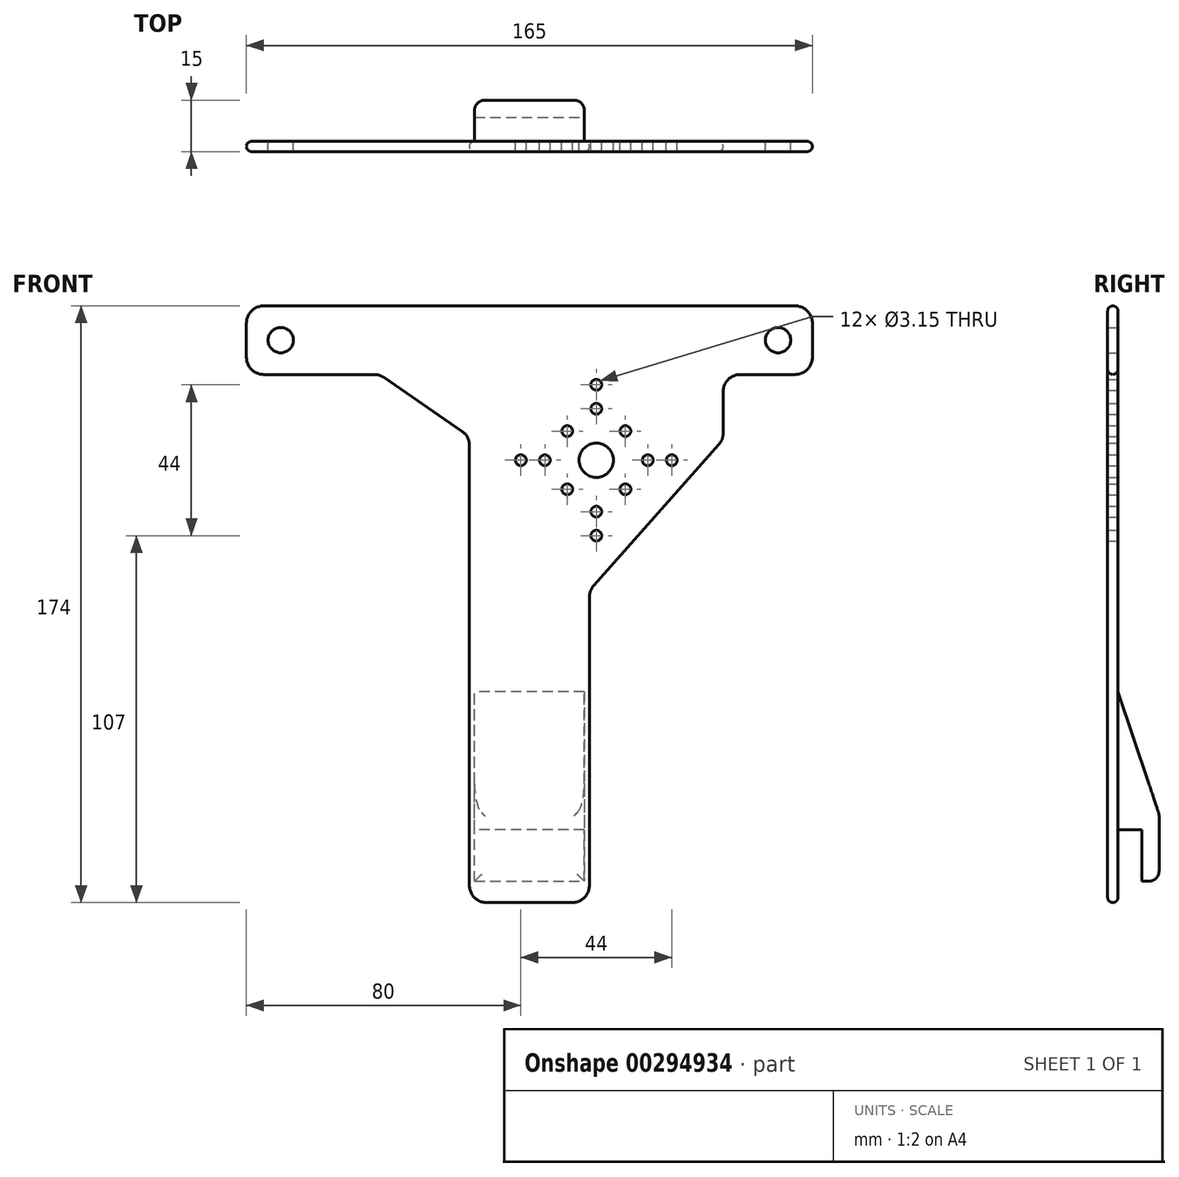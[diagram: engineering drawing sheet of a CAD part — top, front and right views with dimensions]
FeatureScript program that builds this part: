
annotation { "Feature Type Name" : "Feature", "Feature Type Description" : "" }
export const myFeature = defineFeature(function(context is Context, id is Id, definition is map)
    precondition{}
    {
        {
            var Q0;
            Q0=qCreatedBy(makeId("Front.planeOp"),FACE);
            var sketch = newSketch(context, id + "F0", { "sketchPlane" : qUnion([Q0])});
            skPoint(sketch, "E0.middle", {"position": v(0, 0) * mm});
            skLineSegment(sketch, "E1", {"start": v(82.5, 40) * mm, "end": v(-82.5, 40) * mm, "construction": true});
            skCircle(sketch, "E2", {"center": v(19.5, 33) * mm, "radius": 5 * mm});
            skCircle(sketch, "E3", {"center": v(41.5, 33) * mm, "radius": 1.57 * mm});
            skCircle(sketch, "E4", {"center": v(34.5, 33) * mm, "radius": 1.57 * mm});
            skCircle(sketch, "E5", {"center": v(19.5, 11) * mm, "radius": 1.57 * mm});
            skCircle(sketch, "E6", {"center": v(19.5, 18) * mm, "radius": 1.57 * mm});
            skLineSegment(sketch, "E7", {"start": v(19.5, 63.47) * mm, "end": v(19.5, 5.45) * mm, "construction": true});
            skCircle(sketch, "E8.MirrorC", {"center": v(-2.5, 33) * mm, "radius": 1.57 * mm});
            skCircle(sketch, "E9.MirrorC", {"center": v(4.5, 33) * mm, "radius": 1.57 * mm});
            skCircle(sketch, "E10.MirrorC", {"center": v(19.5, 55) * mm, "radius": 1.57 * mm});
            skCircle(sketch, "E11.MirrorC", {"center": v(19.5, 48) * mm, "radius": 1.57 * mm});
            skLineSegment(sketch, "E12", {"start": v(19.5, 40) * mm, "end": v(0.9, 58.6) * mm, "construction": true});
            skCircle(sketch, "E13", {"center": v(11.01, 41.49) * mm, "radius": 1.57 * mm});
            skCircle(sketch, "E14.MirrorC", {"center": v(27.99, 41.49) * mm, "radius": 1.57 * mm});
            skCircle(sketch, "E15.MirrorC", {"center": v(27.99, 24.51) * mm, "radius": 1.57 * mm});
            skCircle(sketch, "E16.MirrorC", {"center": v(11.01, 24.51) * mm, "radius": 1.57 * mm});
            skLineSegment(sketch, "E17", {"start": v(-82.5, -80) * mm, "end": v(82.5, -80) * mm, "construction": true});
            skLineSegment(sketch, "E18", {"start": v(-17.5, -80) * mm, "end": v(-17.5, -91) * mm});
            skLineSegment(sketch, "E19", {"start": v(17.5, -80) * mm, "end": v(17.5, -91) * mm});
            skLineSegment(sketch, "E20", {"start": v(17.5, -80) * mm, "end": v(17.5, -6.9) * mm});
            skLineSegment(sketch, "E21", {"start": v(56.5, 40.9) * mm, "end": v(56.5, 53) * mm});
            skPoint(sketch, "E22.visualSharp", {"position": v(-82.5, 78) * mm});
            skPoint(sketch, "E23.visualSharp", {"position": v(17.5, 0) * mm});
            skLineSegment(sketch, "E24", {"start": v(-12.5, -96) * mm, "end": v(12.5, -96) * mm});
            skPoint(sketch, "E25.visualSharp", {"position": v(-17.5, -96) * mm});
            skArc(sketch, "E25.filletArc", {"start": v(-17.5, -91) * mm, "mid": v(-16.04, -94.54) * mm, "end": v(-12.5, -96) * mm});
            skPoint(sketch, "E26.visualSharp", {"position": v(17.5, -96) * mm});
            skArc(sketch, "E26.filletArc", {"start": v(12.5, -96) * mm, "mid": v(16.04, -94.54) * mm, "end": v(17.5, -91) * mm});
            skLineSegment(sketch, "E27", {"start": v(18.76, -3.58) * mm, "end": v(55.24, 37.58) * mm});
            skPoint(sketch, "E28.visualSharp", {"position": v(56.5, 39) * mm});
            skArc(sketch, "E28.filletArc", {"start": v(55.24, 37.58) * mm, "mid": v(56.17, 39.12) * mm, "end": v(56.5, 40.9) * mm});
            skPoint(sketch, "E29.visualSharp", {"position": v(17.5, -5) * mm});
            skArc(sketch, "E29.filletArc", {"start": v(18.76, -3.58) * mm, "mid": v(17.83, -5.12) * mm, "end": v(17.5, -6.9) * mm});
            skCircle(sketch, "E30", {"center": v(-72.5, 68) * mm, "radius": 3.68 * mm});
            skCircle(sketch, "E31", {"center": v(72.5, 68) * mm, "radius": 3.68 * mm});
            skLineSegment(sketch, "E32", {"start": v(82.5, 73) * mm, "end": v(82.5, 63) * mm});
            skLineSegment(sketch, "E33", {"start": v(-82.5, 73) * mm, "end": v(-82.5, 63) * mm});
            skLineSegment(sketch, "E34", {"start": v(-77.5, 78) * mm, "end": v(77.5, 78) * mm});
            skLineSegment(sketch, "E35.trimOffspring", {"start": v(61.5, 58) * mm, "end": v(77.5, 58) * mm});
            skPoint(sketch, "E36.visualSharp", {"position": v(-82.5, 58) * mm});
            skArc(sketch, "E36.filletArc", {"start": v(-82.5, 63) * mm, "mid": v(-81.04, 59.46) * mm, "end": v(-77.5, 58) * mm});
            skArc(sketch, "E37.filletArc", {"start": v(-77.5, 78) * mm, "mid": v(-81.04, 76.54) * mm, "end": v(-82.5, 73) * mm});
            skPoint(sketch, "E38.visualSharp", {"position": v(82.5, 78) * mm});
            skArc(sketch, "E38.filletArc", {"start": v(82.5, 73) * mm, "mid": v(81.04, 76.54) * mm, "end": v(77.5, 78) * mm});
            skPoint(sketch, "E39.visualSharp", {"position": v(82.5, 58) * mm});
            skArc(sketch, "E39.filletArc", {"start": v(77.5, 58) * mm, "mid": v(81.04, 59.46) * mm, "end": v(82.5, 63) * mm});
            skPoint(sketch, "E40.visualSharp", {"position": v(56.5, 58) * mm});
            skArc(sketch, "E40.filletArc", {"start": v(61.5, 58) * mm, "mid": v(57.96, 56.54) * mm, "end": v(56.5, 53) * mm});
            skLineSegment(sketch, "E41", {"start": v(-77.5, 58) * mm, "end": v(-45.3, 58) * mm});
            skLineSegment(sketch, "E42", {"start": v(-17.5, -80) * mm, "end": v(-17.5, 37.37) * mm});
            skLineSegment(sketch, "E43", {"start": v(-42.47, 57.12) * mm, "end": v(-19.67, 41.49) * mm});
            skPoint(sketch, "E44.visualSharp", {"position": v(-43.75, 58) * mm});
            skArc(sketch, "E44.filletArc", {"start": v(-42.47, 57.12) * mm, "mid": v(-43.82, 57.78) * mm, "end": v(-45.3, 58) * mm});
            skPoint(sketch, "E45.visualSharp", {"position": v(-17.5, 40) * mm});
            skArc(sketch, "E45.filletArc", {"start": v(-17.5, 37.37) * mm, "mid": v(-18.08, 39.7) * mm, "end": v(-19.67, 41.49) * mm});
            skSolve(sketch);
        }
        {
            var Q0;
            Q0=makeQuery(id+"F0.imprint","IMPRINT",FACE,{"disambiguationData":[TD([[makeQuery(id+"F0.imprint","IMPRINT",EDGE,{"derivedFrom":sQuery(id+"F0.wireOp",EDGE,"E0.top")}),1.0]])]});
            var Q1;
            Q1=makeQuery(id+"F0.imprint","IMPRINT",FACE,{"disambiguationData":[TD([[makeQuery(id+"F0.imprint","IMPRINT",EDGE,{"derivedFrom":sQuery(id+"F0.wireOp",EDGE,"E2")}),-1.0]])]});
            extrude(context, id + "F1", {"entities" : qUnion([Q0, Q1]), "depth" : 3 * mm, "offsetDistance" : 25 * mm});
        }
        {
            var Q0;
            Q0=makeQuery(id+"F1.opExtrude","CAP_EDGE",EDGE,{"disambiguationData":[OSD([sQuery(id+"F0.wireOp",EDGE,"E34")])],"isStart":true});
            var Q1;
            Q1=makeQuery(id+"F1.opExtrude","CAP_EDGE",EDGE,{"disambiguationData":[OSD([sQuery(id+"F0.wireOp",EDGE,"E34")])],"isStart":false});
            fillet(context, id + "F2", {"entities" : qUnion([Q0, Q1]), "radius" : 1.5 * mm, "tangentPropagation" : true, "allowEdgeOverflow" : false});
        }
        {
            var Q0;
            Q0=makeQuery(id+"F1.opExtrude","CAP_FACE",FACE,{"disambiguationData":[OSD([sQuery(id+"F0.wireOp",EDGE,"E0.top"),sQuery(id+"F0.wireOp",EDGE,"E2"),sQuery(id+"F0.wireOp",EDGE,"E3"),sQuery(id+"F0.wireOp",EDGE,"E4"),sQuery(id+"F0.wireOp",EDGE,"E5"),sQuery(id+"F0.wireOp",EDGE,"E6"),sQuery(id+"F0.wireOp",EDGE,"E8.MirrorC"),sQuery(id+"F0.wireOp",EDGE,"E9.MirrorC"),sQuery(id+"F0.wireOp",EDGE,"E10.MirrorC"),sQuery(id+"F0.wireOp",EDGE,"E11.MirrorC"),sQuery(id+"F0.wireOp",EDGE,"E13"),sQuery(id+"F0.wireOp",EDGE,"E14.MirrorC"),sQuery(id+"F0.wireOp",EDGE,"E15.MirrorC"),sQuery(id+"F0.wireOp",EDGE,"E16.MirrorC"),sQuery(id+"F0.wireOp",EDGE,"n9Zw0jRa-YzkP-SSRb-jX76-UWUrNYys0Myr"),sQuery(id+"F0.wireOp",EDGE,"6nXTgwqW-IkDt-4185-NQ3I-D9ohkwow1pDC"),sQuery(id+"F0.wireOp",EDGE,"fnSGR3eZ-Ceom-D6FO-QKlf-8HLsdzlY8Ce6"),sQuery(id+"F0.wireOp",EDGE,"E18"),sQuery(id+"F0.wireOp",EDGE,"E19"),sQuery(id+"F0.wireOp",EDGE,"8tiRwyeG-NVE4-zL7y-cv12-UPCtmKI0cug2"),sQuery(id+"F0.wireOp",EDGE,"E20"),sQuery(id+"F0.wireOp",EDGE,"ygad2Ens-O4ax-aDfu-Q5ng-kWepvQ1ZYTQx"),sQuery(id+"F0.wireOp",EDGE,"E21"),sQuery(id+"F0.wireOp",EDGE,"29b9c4b6-7081-4e3b-b4dd-28010079924f.trimOffspring"),sQuery(id+"F0.wireOp",EDGE,"4647f22d-6d82-4992-9f22-0e3dd7c63f78.trimOffspring"),sQuery(id+"F0.wireOp",EDGE,"0a04f032-77e3-4663-9b60-4ac6a7c6c2fa.trimOffspring"),sQuery(id+"F0.wireOp",EDGE,"5f09185c-aee7-4edb-8201-1ebfa4ec7862.filletArc"),sQuery(id+"F0.wireOp",EDGE,"E22.filletArc"),sQuery(id+"F0.wireOp",EDGE,"c5754e04-9c71-4b08-b6d4-417d1572ddd7.filletArc"),sQuery(id+"F0.wireOp",EDGE,"7fc32371-5d91-4005-95ad-299b1605f1e9.filletArc"),sQuery(id+"F0.wireOp",EDGE,"473fdc03-1da2-4e76-872e-939869ff3119.filletArc"),sQuery(id+"F0.wireOp",EDGE,"168d16bf-a7e2-44a5-a079-a20fe12f3d41.filletArc"),sQuery(id+"F0.wireOp",EDGE,"bfc25fbe-79ac-433f-8260-2f5cbf39e1db.filletArc"),sQuery(id+"F0.wireOp",EDGE,"E23.filletArc"),sQuery(id+"F0.wireOp",EDGE,"E24"),sQuery(id+"F0.wireOp",EDGE,"E25.filletArc"),sQuery(id+"F0.wireOp",EDGE,"E26.filletArc")])],"isStart":true});
            var sketch = newSketch(context, id + "F3", { "sketchPlane" : qUnion([Q0])});
            skLineSegment(sketch, "E46", {"start": v(-16, -74.8) * mm, "end": v(16, -74.8) * mm});
            skLineSegment(sketch, "E47", {"start": v(16, -74.8) * mm, "end": v(16, -70.22) * mm});
            skLineSegment(sketch, "E48", {"start": v(16, -70.22) * mm, "end": v(-16, -70.22) * mm});
            skLineSegment(sketch, "E49", {"start": v(-16, -70.22) * mm, "end": v(-16, -74.8) * mm});
            skSolve(sketch);
        }
        {
            var Q0;
            Q0 = qSketchRegion(id + "F3", true);
            extrude(context, id + "F4", {"entities" : qUnion([Q0]), "operationType" : NewBodyOperationType.ADD, "depth" : 12 * mm, "offsetDistance" : 25 * mm});
        }
        {
            var Q0;
            Q0=makeQuery(id+"F4.opExtrude","SWEPT_FACE",FACE,{"disambiguationData":[OSD([sQuery(id+"F3.wireOp",EDGE,"E46")])]});
            var sketch = newSketch(context, id + "F5", { "sketchPlane" : qUnion([Q0])});
            skLineSegment(sketch, "E50.bottom", {"start": v(-16, -12) * mm, "end": v(16, -12) * mm});
            skLineSegment(sketch, "E50.top", {"start": v(-16, -7) * mm, "end": v(16, -7) * mm});
            skLineSegment(sketch, "E50.left", {"start": v(-16, -12) * mm, "end": v(-16, -7) * mm});
            skLineSegment(sketch, "E50.right", {"start": v(16, -12) * mm, "end": v(16, -7) * mm});
            skSolve(sketch);
        }
        {
            var Q0;
            Q0=makeQuery(id+"F5.imprint","IMPRINT",FACE,{"disambiguationData":[TD([[makeQuery(id+"F5.imprint","IMPRINT",EDGE,{"derivedFrom":sQuery(id+"F5.wireOp",EDGE,"E50.bottom")}),-1.0]])]});
            extrude(context, id + "F6", {"entities" : qUnion([Q0]), "operationType" : NewBodyOperationType.ADD, "depth" : 15 * mm});
        }
        {
            var Q0;
            Q0=makeQuery(id+"F6.boolean.opBoolean","MERGE",FACE,{"derivedFrom":[makeQuery(id+"F4.opExtrude","SWEPT_FACE",FACE,{"disambiguationData":[OSD([sQuery(id+"F3.wireOp",EDGE,"E47")])]}),makeQuery(id+"F6.opExtrude","SWEPT_FACE",FACE,{"disambiguationData":[OSD([sQuery(id+"F5.wireOp",EDGE,"E50.left")])]})]});
            var sketch = newSketch(context, id + "F7", { "sketchPlane" : qUnion([Q0])});
            skLineSegment(sketch, "E51", {"start": v(-12, -70.22) * mm, "end": v(0, -34.5) * mm});
            skLineSegment(sketch, "E52", {"start": v(0, -34.5) * mm, "end": v(0, -70.22) * mm});
            skSolve(sketch);
        }
        {
            var Q0;
            Q0=makeQuery(id+"F7.imprint","IMPRINT",FACE,{"disambiguationData":[TD([[makeQuery(id+"F7.imprint","IMPRINT",EDGE,{"derivedFrom":sQuery(id+"F7.wireOp",EDGE,"E51")}),-1.0]])]});
            extrude(context, id + "F8", {"entities" : qUnion([Q0]), "operationType" : NewBodyOperationType.ADD, "oppositeDirection" : true, "depth" : 32 * mm, "offsetDistance" : 25 * mm});
        }
        {
            var Q0;
            {var subQ0=sQuery(id+"F3.wireOp",EDGE,"E48");Q0=makeQuery(id+"F8.boolean.opBoolean","MERGE",EDGE,{"derivedFrom":[makeQuery(id+"F4.opExtrude","CAP_EDGE",EDGE,{"disambiguationData":[OSD([subQ0])],"isStart":false}),makeQuery(id+"F8.opExtrude","SWEPT_EDGE",EDGE,{"disambiguationData":[OSD([sQuery(id+"F0.wireOp",EDGE,"E0.top"),sQuery(id+"F0.wireOp",EDGE,"E2"),sQuery(id+"F0.wireOp",EDGE,"E3"),sQuery(id+"F0.wireOp",EDGE,"E4"),sQuery(id+"F0.wireOp",EDGE,"E5"),sQuery(id+"F0.wireOp",EDGE,"E6"),sQuery(id+"F0.wireOp",EDGE,"E8.MirrorC"),sQuery(id+"F0.wireOp",EDGE,"E9.MirrorC"),sQuery(id+"F0.wireOp",EDGE,"E10.MirrorC"),sQuery(id+"F0.wireOp",EDGE,"E11.MirrorC"),sQuery(id+"F0.wireOp",EDGE,"E13"),sQuery(id+"F0.wireOp",EDGE,"E14.MirrorC"),sQuery(id+"F0.wireOp",EDGE,"E15.MirrorC"),sQuery(id+"F0.wireOp",EDGE,"E16.MirrorC"),sQuery(id+"F0.wireOp",EDGE,"n9Zw0jRa-YzkP-SSRb-jX76-UWUrNYys0Myr"),sQuery(id+"F0.wireOp",EDGE,"6nXTgwqW-IkDt-4185-NQ3I-D9ohkwow1pDC"),sQuery(id+"F0.wireOp",EDGE,"fnSGR3eZ-Ceom-D6FO-QKlf-8HLsdzlY8Ce6"),sQuery(id+"F0.wireOp",EDGE,"E18"),sQuery(id+"F0.wireOp",EDGE,"E19"),sQuery(id+"F0.wireOp",EDGE,"8tiRwyeG-NVE4-zL7y-cv12-UPCtmKI0cug2"),sQuery(id+"F0.wireOp",EDGE,"E20"),sQuery(id+"F0.wireOp",EDGE,"E21"),sQuery(id+"F0.wireOp",EDGE,"29b9c4b6-7081-4e3b-b4dd-28010079924f.trimOffspring"),sQuery(id+"F0.wireOp",EDGE,"4647f22d-6d82-4992-9f22-0e3dd7c63f78.trimOffspring"),sQuery(id+"F0.wireOp",EDGE,"0a04f032-77e3-4663-9b60-4ac6a7c6c2fa.trimOffspring"),sQuery(id+"F0.wireOp",EDGE,"E22.filletArc"),sQuery(id+"F0.wireOp",EDGE,"c5754e04-9c71-4b08-b6d4-417d1572ddd7.filletArc"),sQuery(id+"F0.wireOp",EDGE,"7fc32371-5d91-4005-95ad-299b1605f1e9.filletArc"),sQuery(id+"F0.wireOp",EDGE,"473fdc03-1da2-4e76-872e-939869ff3119.filletArc"),sQuery(id+"F0.wireOp",EDGE,"168d16bf-a7e2-44a5-a079-a20fe12f3d41.filletArc"),sQuery(id+"F0.wireOp",EDGE,"E24"),sQuery(id+"F0.wireOp",EDGE,"E25.filletArc"),sQuery(id+"F0.wireOp",EDGE,"E26.filletArc"),sQuery(id+"F0.wireOp",EDGE,"E27"),sQuery(id+"F0.wireOp",EDGE,"O4lpc8tL-hSbE-3tZc-u3ic-XTAUAKy5I7zL"),sQuery(id+"F0.wireOp",EDGE,"E28.filletArc"),sQuery(id+"F0.wireOp",EDGE,"E29.filletArc"),sQuery(id+"F0.wireOp",EDGE,"0ac6a800-955e-4dc5-aaf9-9da0e2d401f0.filletArc"),sQuery(id+"F0.wireOp",EDGE,"ef82a3f4-a9b0-41f4-8f36-791381020075.filletArc"),sQuery(id+"F3.wireOp",EDGE,"E47"),subQ0,sQuery(id+"F5.wireOp",EDGE,"E50.bottom"),sQuery(id+"F5.wireOp",EDGE,"E50.left"),sQuery(id+"F7.wireOp",EDGE,"E51")])]})]});}
            var Q1;
            Q1=makeQuery(id+"F6.opExtrude","CAP_EDGE",EDGE,{"disambiguationData":[OSD([sQuery(id+"F5.wireOp",EDGE,"E50.top")])],"isStart":true});
            var Q2;
            Q2=makeQuery(id+"F8.opExtrude","SWEPT_EDGE",EDGE,{"disambiguationData":[OSD([sQuery(id+"F7.wireOp",EDGE,"E51"),sQuery(id+"F7.wireOp",EDGE,"E52")])]});
            var Q3;
            Q3=makeQuery(id+"F6.boolean.opBoolean","MERGE",EDGE,{"derivedFrom":[makeQuery(id+"F4.opExtrude","CAP_EDGE",EDGE,{"disambiguationData":[OSD([sQuery(id+"F3.wireOp",EDGE,"E49")])],"isStart":false}),makeQuery(id+"F6.opExtrude","SWEPT_EDGE",EDGE,{"disambiguationData":[OSD([sQuery(id+"F5.wireOp",EDGE,"E50.bottom"),sQuery(id+"F5.wireOp",EDGE,"E50.right")])]})]});
            var Q4;
            Q4=makeQuery(id+"F6.boolean.opBoolean","MERGE",EDGE,{"derivedFrom":[makeQuery(id+"F4.opExtrude","CAP_EDGE",EDGE,{"disambiguationData":[OSD([sQuery(id+"F3.wireOp",EDGE,"E47")])],"isStart":false}),makeQuery(id+"F6.opExtrude","SWEPT_EDGE",EDGE,{"disambiguationData":[OSD([sQuery(id+"F5.wireOp",EDGE,"E50.bottom"),sQuery(id+"F5.wireOp",EDGE,"E50.left")])]})]});
            var Q5;
            Q5=makeQuery(id+"F6.opExtrude","CAP_EDGE",EDGE,{"disambiguationData":[OSD([sQuery(id+"F5.wireOp",EDGE,"E50.bottom")])],"isStart":false});
            fillet(context, id + "F9", {"entities" : qUnion([Q0, Q1, Q2, Q3, Q4, Q5]), "radius" : 3 * mm, "tangentPropagation" : true, "allowEdgeOverflow" : false});
        }
    });
